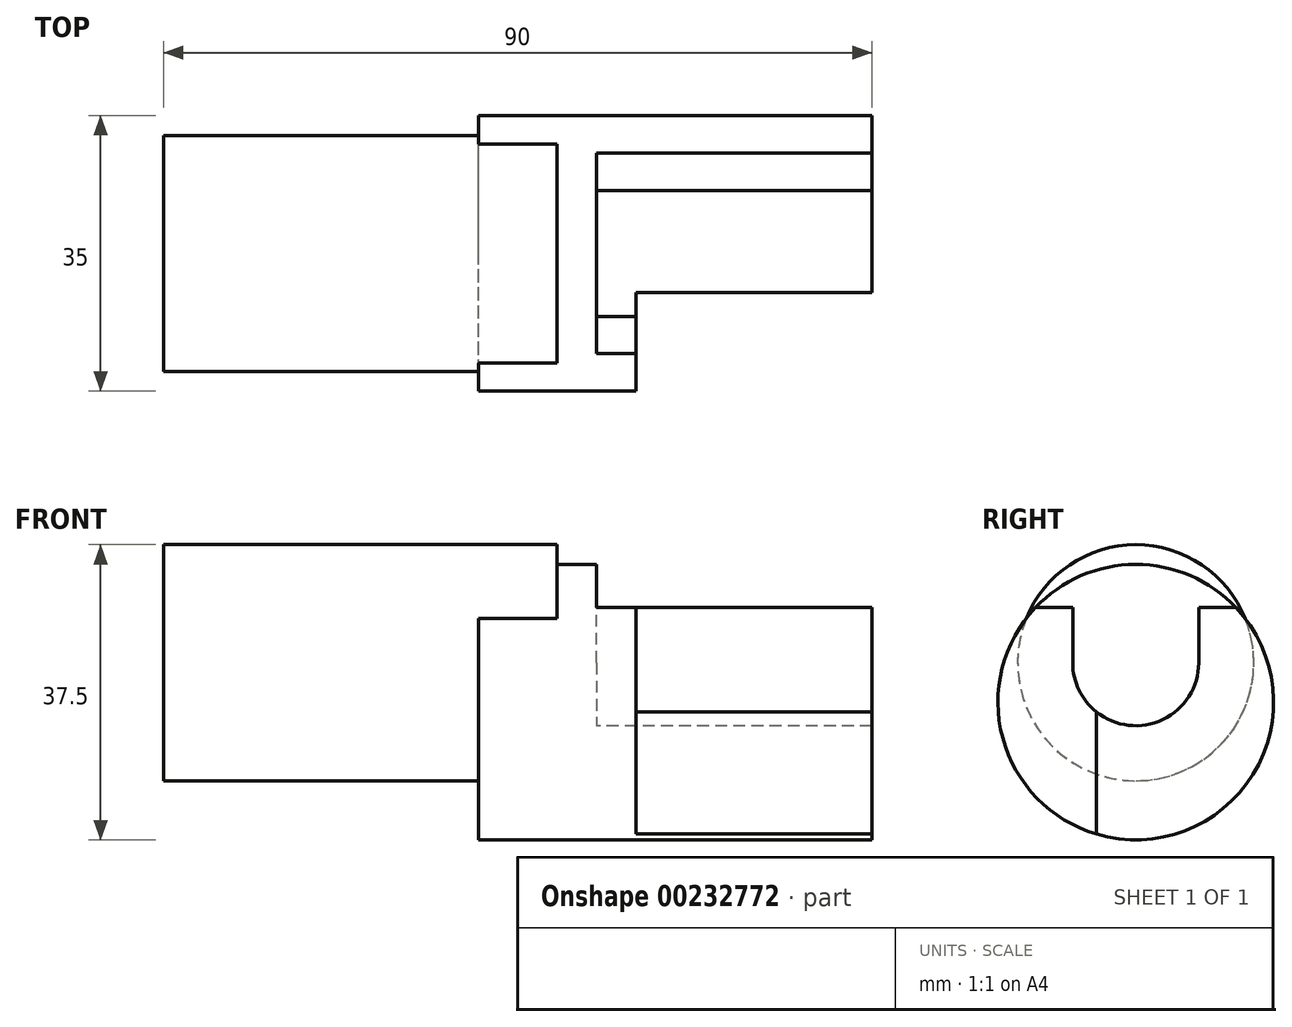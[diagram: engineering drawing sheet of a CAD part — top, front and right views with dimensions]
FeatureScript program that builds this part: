
annotation { "Feature Type Name" : "Feature", "Feature Type Description" : "" }
export const myFeature = defineFeature(function(context is Context, id is Id, definition is map)
    precondition{}
    {
        {
            var Q0;
            Q0=qCreatedBy(makeId("Right.planeOp"),FACE);
            var sketch = newSketch(context, id + "F0", { "sketchPlane" : qUnion([Q0])});
            skCircle(sketch, "E0", {"center": v(33.22, 39.25) * mm, "radius": 17.5 * mm});
            skLineSegment(sketch, "E1", {"start": v(33.22, 62.82) * mm, "end": v(33.22, 25.68) * mm, "construction": true});
            skLineSegment(sketch, "E2", {"start": v(54.57, 39.25) * mm, "end": v(12.4, 39.25) * mm, "construction": true});
            skLineSegment(sketch, "E3", {"start": v(49.16, 44.25) * mm, "end": v(1.27, 44.25) * mm, "construction": true});
            skCircle(sketch, "E4", {"center": v(33.22, 44.25) * mm, "radius": 15 * mm});
            skLineSegment(sketch, "E5", {"start": v(20.48, 51.25) * mm, "end": v(25.22, 51.25) * mm});
            skLineSegment(sketch, "E6", {"start": v(25.22, 51.25) * mm, "end": v(25.22, 44.25) * mm});
            skLineSegment(sketch, "E7", {"start": v(41.22, 44.25) * mm, "end": v(41.22, 51.25) * mm});
            skPoint(sketch, "E7.endSnap0", {"position": v(22.85, 51.25) * mm});
            skLineSegment(sketch, "E8", {"start": v(41.22, 51.25) * mm, "end": v(45.96, 51.25) * mm});
            skArc(sketch, "E9", {"start": v(25.22, 44.25) * mm, "mid": v(33.22, 36.25) * mm, "end": v(41.22, 44.25) * mm});
            skLineSegment(sketch, "E10", {"start": v(28.22, 38) * mm, "end": v(28.22, 22.48) * mm});
            skSolve(sketch);
        }
        {
            var Q0;
            {var subQ0=sQuery(id+"F0.wireOp",EDGE,"E10");var subQ1=sQuery(id+"F0.wireOp",EDGE,"E0");var subQ2=makeQuery(id+"F0.imprint","INTERSECT",VERTEX,{"derivedFrom":[subQ1,subQ0]});Q0=makeQuery(id+"F0.imprint","IMPRINT",FACE,{"disambiguationData":[TD([[makeQuery(id+"F0.imprint","IMPRINT",EDGE,{"disambiguationData":[TD([[subQ2,-1.0]])],"derivedFrom":subQ1}),1.0]])]});}
            var Q1;
            {var subQ1=sQuery(id+"F0.wireOp",EDGE,"E7");Q1=makeQuery(id+"F0.imprint","IMPRINT",FACE,{"disambiguationData":[TD([[makeQuery(id+"F0.imprint","IMPRINT",EDGE,{"derivedFrom":subQ1}),-1.0]])]});}
            extrude(context, id + "F1", {"entities" : qUnion([Q0, Q1]), "depth" : 40 * mm});
        }
        {
            var Q0;
            {var subQ1=sQuery(id+"F0.wireOp",EDGE,"E5");Q0=makeQuery(id+"F0.imprint","IMPRINT",FACE,{"disambiguationData":[TD([[makeQuery(id+"F0.imprint","IMPRINT",EDGE,{"derivedFrom":subQ1}),-1.0]])]});}
            var Q1;
            {var subQ0=sQuery(id+"F0.wireOp",EDGE,"E0");var subQ1=makeQuery(id+"F0.imprint","INTERSECT",VERTEX,{"derivedFrom":[subQ0,sQuery(id+"F0.wireOp",EDGE,"E8")]});Q1=makeQuery(id+"F0.imprint","IMPRINT",FACE,{"disambiguationData":[TD([[makeQuery(id+"F0.imprint","IMPRINT",EDGE,{"disambiguationData":[TD([[subQ1,1.0]])],"derivedFrom":subQ0}),-1.0]])]});}
            var Q2;
            {var subQ2=sQuery(id+"F0.wireOp",EDGE,"E5");Q2=makeQuery(id+"F0.imprint","IMPRINT",FACE,{"disambiguationData":[TD([[makeQuery(id+"F0.imprint","IMPRINT",EDGE,{"derivedFrom":subQ2}),1.0]])]});}
            var Q3;
            {var subQ1=sQuery(id+"F0.wireOp",EDGE,"E7");Q3=makeQuery(id+"F0.imprint","IMPRINT",FACE,{"disambiguationData":[TD([[makeQuery(id+"F0.imprint","IMPRINT",EDGE,{"derivedFrom":subQ1}),-1.0]])]});}
            extrude(context, id + "F2", {"entities" : qUnion([Q0, Q1, Q2, Q3]), "operationType" : NewBodyOperationType.ADD, "oppositeDirection" : true, "depth" : 50 * mm});
        }
        {
            var Q0;
            {var subQ1=sQuery(id+"F0.wireOp",EDGE,"E5");Q0=makeQuery(id+"F0.imprint","IMPRINT",FACE,{"disambiguationData":[TD([[makeQuery(id+"F0.imprint","IMPRINT",EDGE,{"derivedFrom":subQ1}),-1.0]])]});}
            var Q1;
            {var subQ0=sQuery(id+"F0.wireOp",EDGE,"E10");var subQ1=sQuery(id+"F0.wireOp",EDGE,"E0");var subQ2=makeQuery(id+"F0.imprint","INTERSECT",VERTEX,{"derivedFrom":[subQ1,subQ0]});Q1=makeQuery(id+"F0.imprint","IMPRINT",FACE,{"disambiguationData":[TD([[makeQuery(id+"F0.imprint","IMPRINT",EDGE,{"disambiguationData":[TD([[subQ2,1.0]])],"derivedFrom":subQ1}),1.0]])]});}
            extrude(context, id + "F3", {"entities" : qUnion([Q0, Q1]), "operationType" : NewBodyOperationType.ADD, "depth" : 10 * mm});
        }
        {
            var Q0;
            {var subQ2=sQuery(id+"F0.wireOp",EDGE,"E5");Q0=makeQuery(id+"F0.imprint","IMPRINT",FACE,{"disambiguationData":[TD([[makeQuery(id+"F0.imprint","IMPRINT",EDGE,{"derivedFrom":subQ2}),1.0]])]});}
            extrude(context, id + "F4", {"entities" : qUnion([Q0]), "operationType" : NewBodyOperationType.ADD, "depth" : 5 * mm});
        }
        {
            var Q0;
            {var subQ0=sQuery(id+"F0.wireOp",EDGE,"E10");var subQ1=sQuery(id+"F0.wireOp",EDGE,"E0");var subQ2=makeQuery(id+"F0.imprint","INTERSECT",VERTEX,{"derivedFrom":[subQ1,subQ0]});Q0=makeQuery(id+"F0.imprint","IMPRINT",FACE,{"disambiguationData":[TD([[makeQuery(id+"F0.imprint","IMPRINT",EDGE,{"disambiguationData":[TD([[subQ2,1.0]])],"derivedFrom":subQ1}),1.0]])]});}
            var Q1;
            {var subQ0=sQuery(id+"F0.wireOp",EDGE,"E10");var subQ1=sQuery(id+"F0.wireOp",EDGE,"E0");var subQ2=makeQuery(id+"F0.imprint","INTERSECT",VERTEX,{"derivedFrom":[subQ1,subQ0]});Q1=makeQuery(id+"F0.imprint","IMPRINT",FACE,{"disambiguationData":[TD([[makeQuery(id+"F0.imprint","IMPRINT",EDGE,{"disambiguationData":[TD([[subQ2,-1.0]])],"derivedFrom":subQ1}),1.0]])]});}
            extrude(context, id + "F5", {"entities" : qUnion([Q0, Q1]), "operationType" : NewBodyOperationType.ADD, "oppositeDirection" : true, "depth" : 10 * mm});
        }
    });
